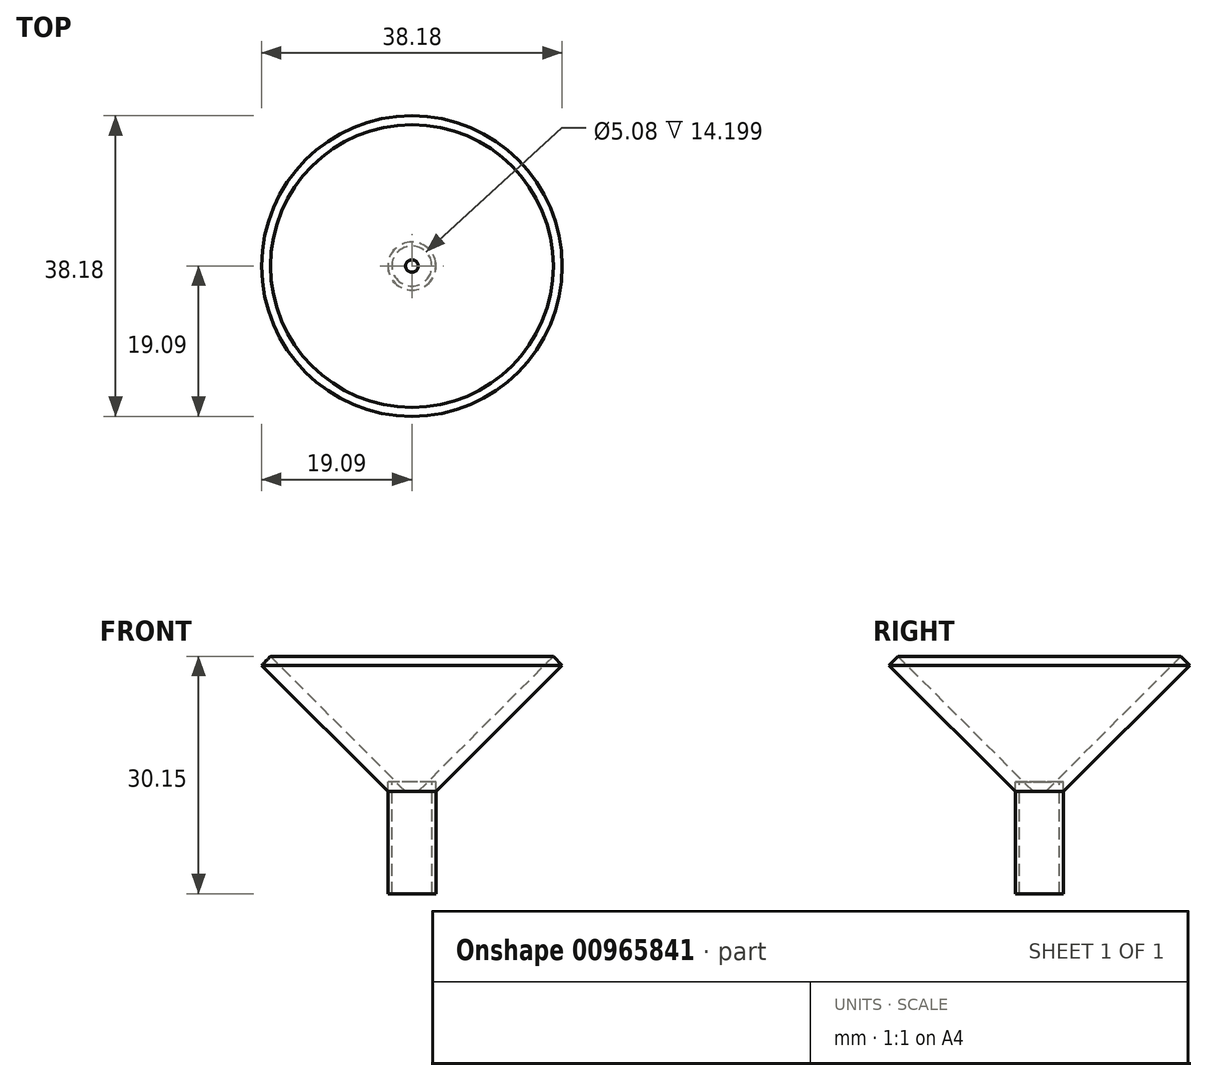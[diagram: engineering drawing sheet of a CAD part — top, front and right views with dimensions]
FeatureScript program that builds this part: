
annotation { "Feature Type Name" : "Feature", "Feature Type Description" : "" }
export const myFeature = defineFeature(function(context is Context, id is Id, definition is map)
    precondition{}
    {
        {
            var Q0;
            Q0=qCreatedBy(makeId("Front.planeOp"),FACE);
            var sketch = newSketch(context, id + "F0", { "sketchPlane" : qUnion([Q0])});
            skLineSegment(sketch, "E0.bottom", {"start": v(-3.18, 0.8) * mm, "end": v(-3.06, 0.8) * mm, "construction": true});
            skLineSegment(sketch, "E0.top", {"start": v(-3.18, -0.8) * mm, "end": v(3.18, -0.8) * mm, "construction": true});
            skLineSegment(sketch, "E0.left", {"start": v(-3.17, 0.8) * mm, "end": v(-3.18, -0.8) * mm, "construction": true});
            skLineSegment(sketch, "E0.right", {"start": v(3.18, 0.8) * mm, "end": v(3.18, -0.8) * mm, "construction": true});
            skPoint(sketch, "E0.middle", {"position": v(0, 0) * mm});
            skLineSegment(sketch, "E1", {"start": v(-3.18, -0.8) * mm, "end": v(-41.28, -0.8) * mm, "construction": true});
            skLineSegment(sketch, "E2", {"start": v(-0.8, 0.8) * mm, "end": v(-17.96, 17.96) * mm});
            skLineSegment(sketch, "E3", {"start": v(-17.96, 17.96) * mm, "end": v(-19.1, 16.83) * mm});
            skLineSegment(sketch, "E4", {"start": v(-19.1, 16.83) * mm, "end": v(-3.06, 0.8) * mm});
            skLineSegment(sketch, "E5", {"start": v(0, -0.8) * mm, "end": v(0, 24.6) * mm, "construction": true});
            skPoint(sketch, "E6.orphan", {"position": v(-2.26, 0) * mm});
            skLineSegment(sketch, "E7.trimOffspring", {"start": v(-0.8, 0.8) * mm, "end": v(3.18, 0.8) * mm, "construction": true});
            skLineSegment(sketch, "E8", {"start": v(-3.06, 0.8) * mm, "end": v(-0.8, 0.8) * mm});
            skLineSegment(sketch, "E9.MirrorCS", {"start": v(0.8, 0.8) * mm, "end": v(17.96, 17.96) * mm});
            skLineSegment(sketch, "E10.MirrorCS", {"start": v(17.96, 17.96) * mm, "end": v(19.1, 16.83) * mm});
            skLineSegment(sketch, "E11.MirrorCS", {"start": v(19.1, 16.83) * mm, "end": v(3.06, 0.8) * mm});
            skLineSegment(sketch, "E12.MirrorCS", {"start": v(3.06, 0.8) * mm, "end": v(0.8, 0.8) * mm});
            skSolve(sketch);
        }
        {
            var Q0;
            Q0=makeQuery(id+"F0.imprint","IMPRINT",FACE,{"disambiguationData":[TD([[makeQuery(id+"F0.imprint","IMPRINT",EDGE,{"derivedFrom":sQuery(id+"F0.wireOp",EDGE,"E9.MirrorCS")}),-1.0]])]});
            var Q1;
            Q1=makeQuery(id+"F0.imprint","IMPRINT",FACE,{"disambiguationData":[TD([[makeQuery(id+"F0.imprint","IMPRINT",EDGE,{"derivedFrom":sQuery(id+"F0.wireOp",EDGE,"E2")}),1.0]])]});
            var Q2;
            Q2=sQuery(id+"F0.wireOp",EDGE,"E5");
            revolve(context, id + "F1", {"surfaceOperationType" : NewSurfaceOperationType.NEW, "entities" : qUnion([Q0, Q1]), "axis" : qUnion([Q2]), "revolveType" : RevolveType.FULL});
        }
        {
            var Q0;
            Q0=qCreatedBy(makeId("Top.planeOp"),FACE);
            var sketch = newSketch(context, id + "F2", { "sketchPlane" : qUnion([Q0])});
            skCircle(sketch, "E13", {"center": v(0, 0) * mm, "radius": 2.54 * mm});
            skCircle(sketch, "E14", {"center": v(0, 0) * mm, "radius": 3.05 * mm});
            skSolve(sketch);
        }
        {
            var Q0;
            Q0=makeQuery(id+"F2.imprint","IMPRINT",FACE,{"disambiguationData":[TD([[makeQuery(id+"F2.imprint","IMPRINT",EDGE,{"derivedFrom":sQuery(id+"F2.wireOp",EDGE,"E13")}),-1.0]])]});
            extrude(context, id + "F3", {"entities" : qUnion([Q0]), "depth" : -12.2 * mm, "offsetDistance" : 25.4 * mm, "hasSecondDirection" : true, "secondDirectionOppositeDirection" : false, "secondDirectionDepth" : 2 * mm});
        }
        {
            var Q0;
            Q0=makeQuery(id+"F1.opRevolve","SWEPT_FACE",FACE,{"disambiguationData":[OSD([sQuery(id+"F0.wireOp",EDGE,"E8")])]});
            var sketch = newSketch(context, id + "F4", { "sketchPlane" : qUnion([Q0])});
            skCircle(sketch, "E15", {"center": v(0, 0) * mm, "radius": 0.8 * mm});
            skSolve(sketch);
        }
        {
            var Q0;
            Q0=makeQuery(id+"F4.imprint","IMPRINT",FACE,{"disambiguationData":[TD([[makeQuery(id+"F4.imprint","IMPRINT",EDGE,{"derivedFrom":sQuery(id+"F4.wireOp",EDGE,"E15")}),1.0]])]});
            extrude(context, id + "F5", {"entities" : qUnion([Q0]), "depth" : 0.04 * mm, "offsetDistance" : 25.4 * mm});
        }
    });
